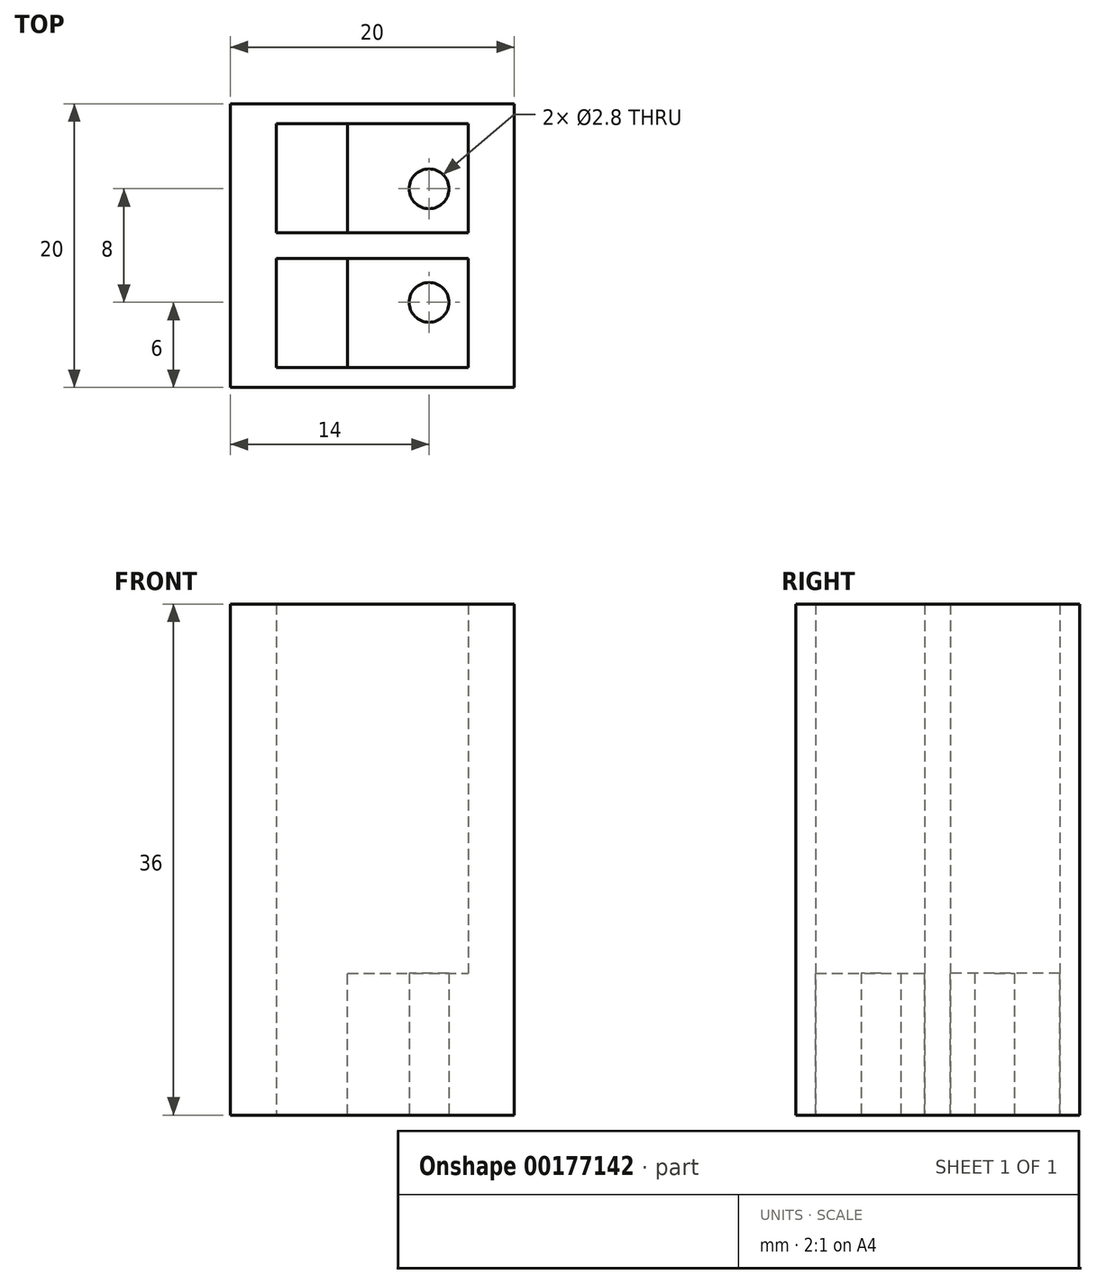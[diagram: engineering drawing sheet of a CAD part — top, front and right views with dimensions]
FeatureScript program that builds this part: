
annotation { "Feature Type Name" : "Feature", "Feature Type Description" : "" }
export const myFeature = defineFeature(function(context is Context, id is Id, definition is map)
    precondition{}
    {
        {
            var Q0;
            Q0=qCreatedBy(makeId("Top.planeOp"),FACE);
            var sketch = newSketch(context, id + "F0", { "sketchPlane" : qUnion([Q0])});
            skLineSegment(sketch, "E0.bottom", {"start": v(10, -10) * mm, "end": v(-10, -10) * mm});
            skLineSegment(sketch, "E0.top", {"start": v(10, 10) * mm, "end": v(-10, 10) * mm});
            skLineSegment(sketch, "E0.left", {"start": v(10, -10) * mm, "end": v(10, 10) * mm});
            skLineSegment(sketch, "E0.right", {"start": v(-10, -10) * mm, "end": v(-10, 10) * mm});
            skPoint(sketch, "E0.middle", {"position": v(0, 0) * mm});
            skLineSegment(sketch, "E1.bottom", {"start": v(6.75, -8.6) * mm, "end": v(-6.75, -8.6) * mm});
            skLineSegment(sketch, "E1.top", {"start": v(6.75, 8.6) * mm, "end": v(-6.75, 8.6) * mm});
            skLineSegment(sketch, "E1.left", {"start": v(6.75, -8.6) * mm, "end": v(6.75, 8.6) * mm});
            skLineSegment(sketch, "E1.right", {"start": v(-6.75, -8.6) * mm, "end": v(-6.75, 8.6) * mm});
            skSolve(sketch);
        }
        {
            var Q0;
            Q0 = qSketchRegion(id + "F0", true);
            extrude(context, id + "F1", {"entities" : qUnion([Q0]), "depth" : 26 * mm});
        }
        {
            var Q0;
            Q0=qCreatedBy(makeId("Top.planeOp"),FACE);
            var sketch = newSketch(context, id + "F2", { "sketchPlane" : qUnion([Q0])});
            skLineSegment(sketch, "E2.bottom", {"start": v(-6.75, 8.6) * mm, "end": v(-1.75, 8.6) * mm});
            skLineSegment(sketch, "E2.top", {"start": v(-6.75, -8.6) * mm, "end": v(-1.75, -8.6) * mm});
            skLineSegment(sketch, "E2.left", {"start": v(-6.75, 8.6) * mm, "end": v(-6.75, -8.6) * mm});
            skLineSegment(sketch, "E2.right", {"start": v(-1.75, 8.6) * mm, "end": v(-1.75, -8.6) * mm});
            skLineSegment(sketch, "E3.bottom", {"start": v(10, 10) * mm, "end": v(-10, 10) * mm});
            skLineSegment(sketch, "E3.top", {"start": v(10, -10) * mm, "end": v(-10, -10) * mm});
            skLineSegment(sketch, "E3.left", {"start": v(10, 10) * mm, "end": v(10, -10) * mm});
            skLineSegment(sketch, "E3.right", {"start": v(-10, 10) * mm, "end": v(-10, -10) * mm});
            skPoint(sketch, "E3.middle", {"position": v(0, 0) * mm});
            skSolve(sketch);
        }
        {
            var Q0;
            Q0 = qSketchRegion(id + "F2", true);
            extrude(context, id + "F3", {"entities" : qUnion([Q0]), "operationType" : NewBodyOperationType.ADD, "oppositeDirection" : true, "depth" : 10 * mm});
        }
        {
            var Q0;
            Q0=makeQuery(id+"F3.opExtrude","CAP_FACE",FACE,{"disambiguationData":[OSD([sQuery(id+"F2.wireOp",EDGE,"E2.bottom"),sQuery(id+"F2.wireOp",EDGE,"E2.top"),sQuery(id+"F2.wireOp",EDGE,"E2.left"),sQuery(id+"F2.wireOp",EDGE,"E2.right"),sQuery(id+"F2.wireOp",EDGE,"E3.bottom"),sQuery(id+"F2.wireOp",EDGE,"E3.top"),sQuery(id+"F2.wireOp",EDGE,"E3.left"),sQuery(id+"F2.wireOp",EDGE,"E3.right")])],"isStart":false});
            var sketch = newSketch(context, id + "F4", { "sketchPlane" : qUnion([Q0])});
            skCircle(sketch, "E4", {"center": v(4, 4) * mm, "radius": 1.4 * mm});
            skCircle(sketch, "E5", {"center": v(4, -4) * mm, "radius": 1.4 * mm});
            skSolve(sketch);
        }
        {
            var Q0;
            Q0 = qSketchRegion(id + "F4", true);
            extrude(context, id + "F5", {"entities" : qUnion([Q0]), "operationType" : NewBodyOperationType.REMOVE, "oppositeDirection" : true, "depth" : 25 * mm});
        }
        {
            var Q0;
            Q0=makeQuery(id+"F3.opExtrude","CAP_FACE",FACE,{"disambiguationData":[OSD([sQuery(id+"F2.wireOp",EDGE,"E2.bottom"),sQuery(id+"F2.wireOp",EDGE,"E2.top"),sQuery(id+"F2.wireOp",EDGE,"E2.left"),sQuery(id+"F2.wireOp",EDGE,"E2.right"),sQuery(id+"F2.wireOp",EDGE,"E3.bottom"),sQuery(id+"F2.wireOp",EDGE,"E3.top"),sQuery(id+"F2.wireOp",EDGE,"E3.left"),sQuery(id+"F2.wireOp",EDGE,"E3.right")])],"isStart":false});
            var sketch = newSketch(context, id + "F6", { "sketchPlane" : qUnion([Q0])});
            skLineSegment(sketch, "E6.bottom", {"start": v(6.75, -0.9) * mm, "end": v(-6.75, -0.9) * mm});
            skLineSegment(sketch, "E6.top", {"start": v(6.75, 0.9) * mm, "end": v(-6.75, 0.9) * mm});
            skLineSegment(sketch, "E6.left", {"start": v(6.75, -0.9) * mm, "end": v(6.75, 0.9) * mm});
            skLineSegment(sketch, "E6.right", {"start": v(-6.75, -0.9) * mm, "end": v(-6.75, 0.9) * mm});
            skPoint(sketch, "E6.middle", {"position": v(0, 0) * mm});
            skSolve(sketch);
        }
        {
            var Q0;
            Q0 = qSketchRegion(id + "F6", true);
            extrude(context, id + "F7", {"entities" : qUnion([Q0]), "operationType" : NewBodyOperationType.ADD, "oppositeDirection" : true, "depth" : 36 * mm});
        }
    });
